# Revit family: AH66-12T-BSG
name_source: partatom
category: Communication Devices
revit_build: Autodesk Revit 2014 (Build: 20140709_2115(x64)
units: mm (PartAtom-declared; Revit-internal decimal feet)

## types (1)
- Full-Range, Outdoor, Horn Loudspeaker
    70V Taps = 7.5, 15, 30 &, 60 watts
    Baffle Material = <By Category>
    Body Material = Default
    Color = <By Category>
    Cost = 1433.99 $
    Cost MSRP = 1433.99 $
    Coverage Horizontal = 65.00°
    Coverage Vertical = 0.00°
    Depth = 21.25 "
    Description = 12" 2-WAY STADIUM HORN LOUDSPEAKER SYSTEM 65° X 65°
    Dispersion Angle = 65.00°
    Enclosure Material = <By Category>
    Family Code (default) = LOUD SPEAKERS
    Frequency Response  = 80Hz - 15kHz (±5dB)
    Grill Material = QF_Plastic - Black - Fine Textured
    HF Driver = 65° H x 65°V HF Horn
    Height = 23.88 "
    IQ Category = SPEAKERS
    Impedance = 8
    Ingress Protection = IP45 When Tilted 5° Downwards
    Manufacturer = ATLAS SOUND
    Manufacturer URL = https://www.atlasied.com
    Market = Commercial, Higher Education, Emergency
    MasterFormat = 27 41 13
    MaterFormat Title = SPEAKERS
    Model = AH66-12T-BSG
    Mount Material = Default
    OmniClass Number = 23-37 17 13 19
    OmniClass Title = SPEAKERS
    Pitch = 0.00°
    Power Rating (RMS) = 200 watts
    Product Documentation Link = https://www.atlasied.com
    Product Page URL = https://www.atlasied.com
    Rotation = 0.00°
    SPL Max = 107
    ScheduleType |RF| = AtlasIED Master
    Sensitivity = 101
    Speaker Dispersion = 65.00°
    Transformer Option = Yes
    URL = www.atlassound.com
    Vertical Symmetry = Yes
    Warranty = 5 Year
    Weight Product = 82
    Width = 18.46 "

## geometry (parser evidence)
native form markers: Blend x6, Sweep x4
no freeform markers — native parametric forms only
